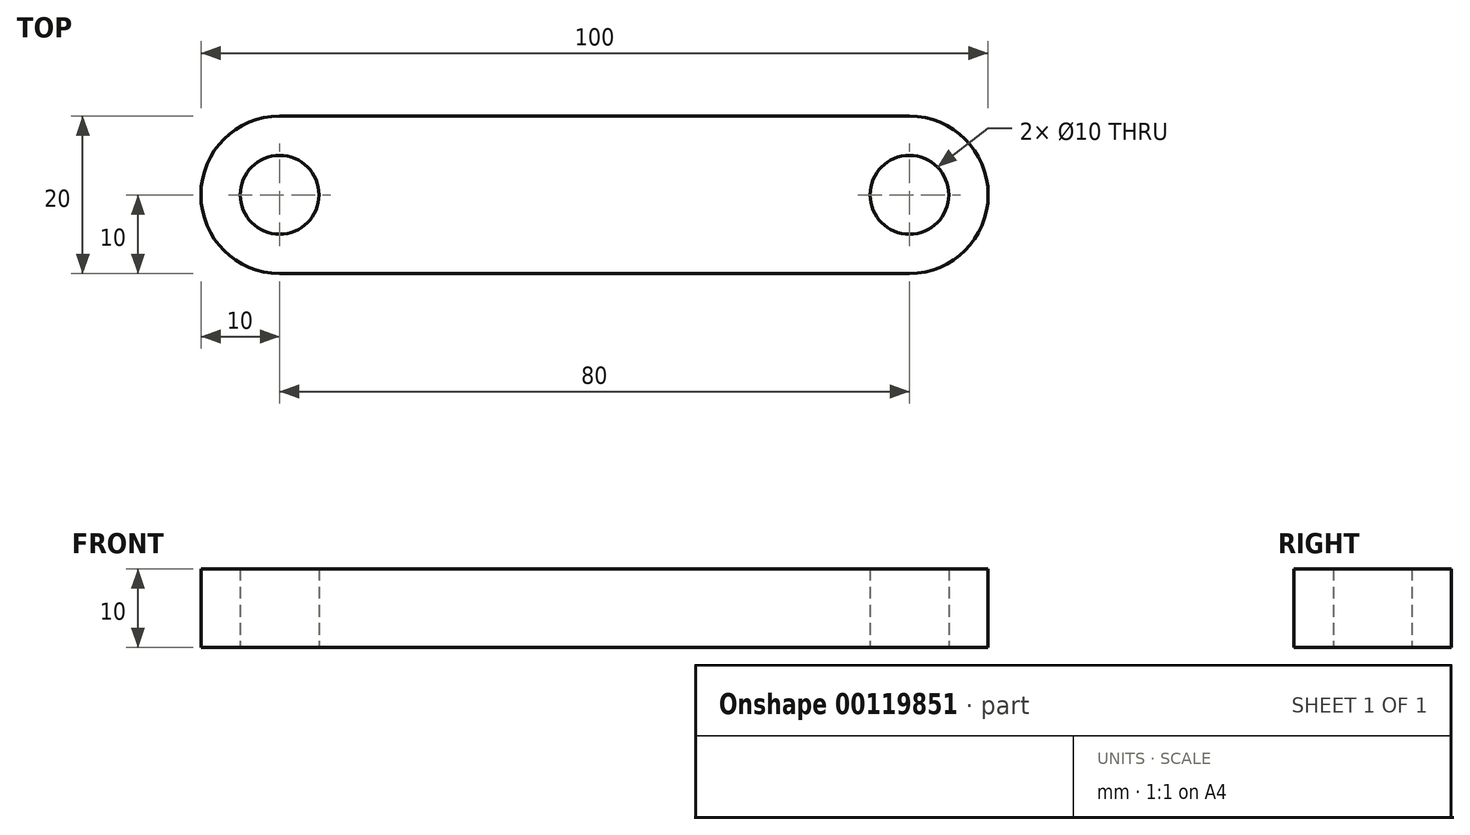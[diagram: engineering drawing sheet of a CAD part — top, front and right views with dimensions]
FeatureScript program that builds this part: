
annotation { "Feature Type Name" : "Feature", "Feature Type Description" : "" }
export const myFeature = defineFeature(function(context is Context, id is Id, definition is map)
    precondition{}
    {
        {
            var Q0;
            Q0=qCreatedBy(makeId("Top.planeOp"),FACE);
            var sketch = newSketch(context, id + "F0", { "sketchPlane" : qUnion([Q0])});
            skCircle(sketch, "E0", {"center": v(0, 0) * mm, "radius": 5 * mm});
            skCircle(sketch, "E1", {"center": v(80, 0) * mm, "radius": 5 * mm});
            skLineSegment(sketch, "E2", {"start": v(0, 10) * mm, "end": v(80, 10) * mm});
            skLineSegment(sketch, "E3", {"start": v(0, -10) * mm, "end": v(80, -10) * mm});
            skArc(sketch, "E4", {"start": v(0, -10) * mm, "mid": v(-10, 0) * mm, "end": v(0, 10) * mm});
            skArc(sketch, "E5", {"start": v(80, 10) * mm, "mid": v(90, 0) * mm, "end": v(80, -10) * mm});
            skSolve(sketch);
        }
        {
            var Q0;
            Q0 = qSketchRegion(id + "F0", true);
            extrude(context, id + "F1", {"entities" : qUnion([Q0]), "depth" : 10 * mm});
        }
    });
